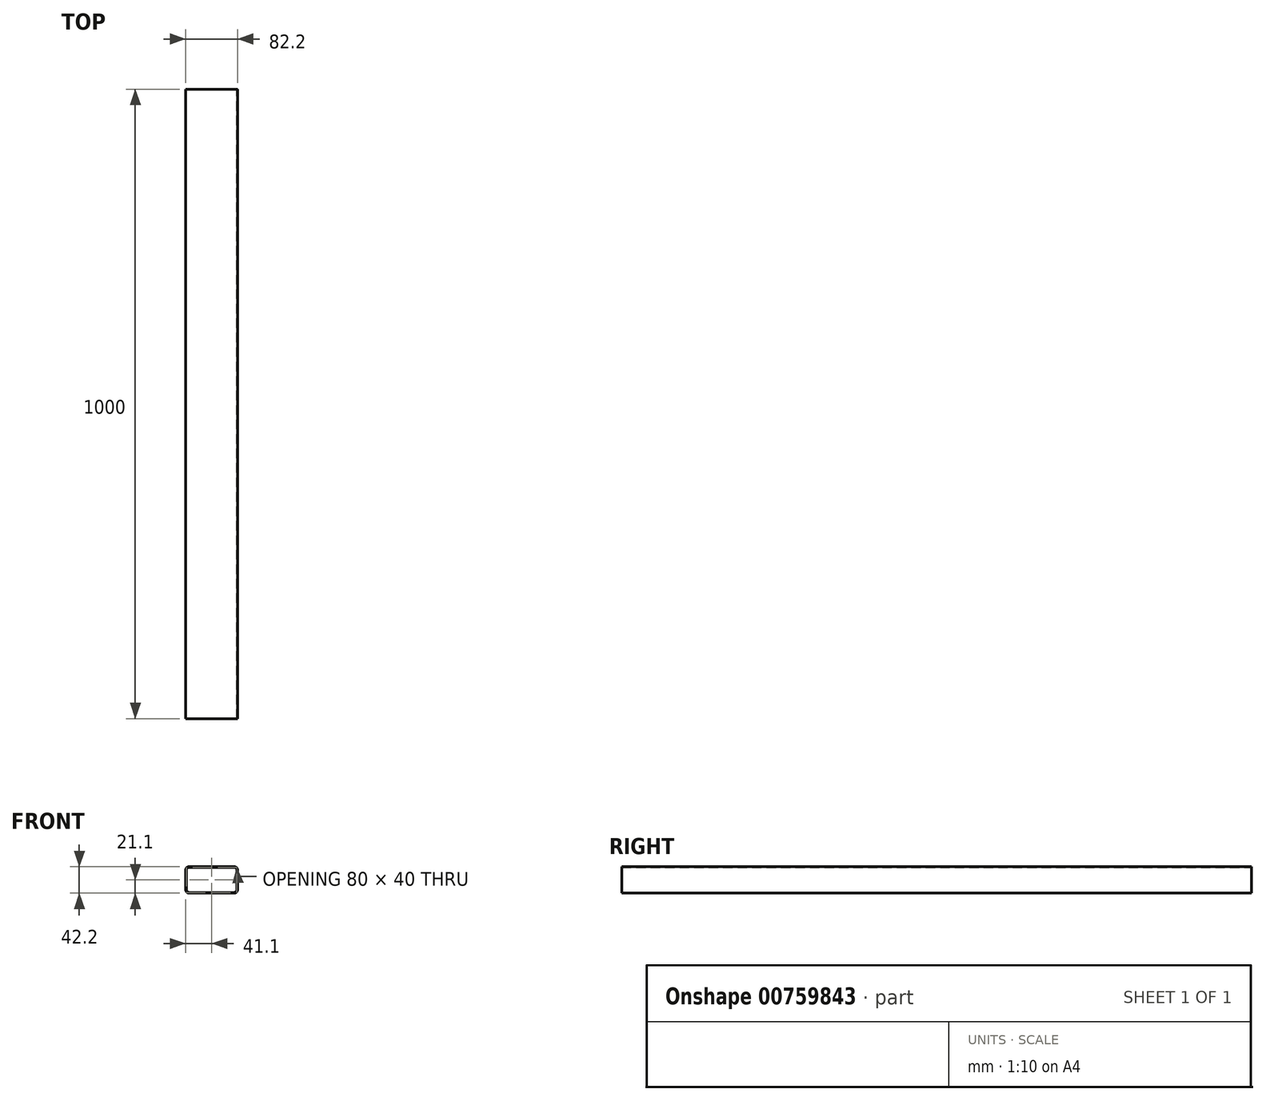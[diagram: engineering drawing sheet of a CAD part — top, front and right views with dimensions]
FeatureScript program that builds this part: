
annotation { "Feature Type Name" : "Feature", "Feature Type Description" : "" }
export const myFeature = defineFeature(function(context is Context, id is Id, definition is map)
    precondition{}
    {
        {
            var Q0;
            Q0=qCreatedBy(makeId("Front.planeOp"),FACE);
            var sketch = newSketch(context, id + "F0", { "sketchPlane" : qUnion([Q0])});
            skLineSegment(sketch, "E0.bottom", {"start": v(-35, 20) * mm, "end": v(35, 20) * mm});
            skLineSegment(sketch, "E0.top", {"start": v(-35, -20) * mm, "end": v(35, -20) * mm});
            skLineSegment(sketch, "E0.left", {"start": v(-40, 15) * mm, "end": v(-40, -15) * mm});
            skLineSegment(sketch, "E0.right", {"start": v(40, 15) * mm, "end": v(40, -15) * mm});
            skPoint(sketch, "E1.visualSharp", {"position": v(-40, 20) * mm});
            skArc(sketch, "E1.filletArc", {"start": v(-35, 20) * mm, "mid": v(-38.54, 18.54) * mm, "end": v(-40, 15) * mm});
            skPoint(sketch, "E2.visualSharp", {"position": v(40, 20) * mm});
            skArc(sketch, "E2.filletArc", {"start": v(40, 15) * mm, "mid": v(38.54, 18.54) * mm, "end": v(35, 20) * mm});
            skPoint(sketch, "E3.visualSharp", {"position": v(40, -20) * mm});
            skArc(sketch, "E3.filletArc", {"start": v(35, -20) * mm, "mid": v(38.54, -18.54) * mm, "end": v(40, -15) * mm});
            skPoint(sketch, "E4.visualSharp", {"position": v(-40, -20) * mm});
            skArc(sketch, "E4.filletArc", {"start": v(-40, -15) * mm, "mid": v(-38.54, -18.54) * mm, "end": v(-35, -20) * mm});
            skLineSegment(sketch, "E5.0", {"start": v(41.1, 16.1) * mm, "end": v(41.1, -16.1) * mm});
            skLineSegment(sketch, "E5.1", {"start": v(-36.1, 21.1) * mm, "end": v(36.1, 21.1) * mm});
            skLineSegment(sketch, "E5.2", {"start": v(-41.1, 16.1) * mm, "end": v(-41.1, -16.1) * mm});
            skLineSegment(sketch, "E5.3", {"start": v(-36.1, -21.1) * mm, "end": v(36.1, -21.1) * mm});
            skPoint(sketch, "E6.visualSharp", {"position": v(-41.1, 21.1) * mm});
            skArc(sketch, "E6.filletArc", {"start": v(-36.1, 21.1) * mm, "mid": v(-39.64, 19.64) * mm, "end": v(-41.1, 16.1) * mm});
            skPoint(sketch, "E7.visualSharp", {"position": v(41.1, 21.1) * mm});
            skArc(sketch, "E7.filletArc", {"start": v(41.1, 16.1) * mm, "mid": v(39.64, 19.64) * mm, "end": v(36.1, 21.1) * mm});
            skPoint(sketch, "E8.visualSharp", {"position": v(41.1, -21.1) * mm});
            skArc(sketch, "E8.filletArc", {"start": v(36.1, -21.1) * mm, "mid": v(39.64, -19.64) * mm, "end": v(41.1, -16.1) * mm});
            skPoint(sketch, "E9.visualSharp", {"position": v(-41.1, -21.1) * mm});
            skArc(sketch, "E9.filletArc", {"start": v(-41.1, -16.1) * mm, "mid": v(-39.64, -19.64) * mm, "end": v(-36.1, -21.1) * mm});
            skSolve(sketch);
        }
        {
            var Q0;
            Q0=makeQuery(id+"F0.imprint","IMPRINT",FACE,{"disambiguationData":[TD([[makeQuery(id+"F0.imprint","IMPRINT",EDGE,{"derivedFrom":sQuery(id+"F0.wireOp",EDGE,"E0.bottom")}),1.0]])]});
            extrude(context, id + "F1", {"entities" : qUnion([Q0]), "depth" : 1000 * mm, "offsetDistance" : 25 * mm});
        }
        {
            var Q0;
            Q0=qCreatedBy(makeId("Front.planeOp"),FACE);
            var sketch = newSketch(context, id + "F2", { "sketchPlane" : qUnion([Q0])});
            skPoint(sketch, "E10", {"position": v(0, 0) * mm});
            skSolve(sketch);
        }
        {
            var Q0;
            Q0=makeQuery(id+"F1.opExtrude","CAP_FACE",FACE,{"disambiguationData":[OSD([sQuery(id+"F0.wireOp",EDGE,"E0.bottom"),sQuery(id+"F0.wireOp",EDGE,"E0.top"),sQuery(id+"F0.wireOp",EDGE,"E0.left"),sQuery(id+"F0.wireOp",EDGE,"E0.right"),sQuery(id+"F0.wireOp",EDGE,"E1.filletArc"),sQuery(id+"F0.wireOp",EDGE,"E2.filletArc"),sQuery(id+"F0.wireOp",EDGE,"E3.filletArc"),sQuery(id+"F0.wireOp",EDGE,"E4.filletArc"),sQuery(id+"F0.wireOp",EDGE,"E5.0"),sQuery(id+"F0.wireOp",EDGE,"E5.1"),sQuery(id+"F0.wireOp",EDGE,"E5.2"),sQuery(id+"F0.wireOp",EDGE,"E5.3"),sQuery(id+"F0.wireOp",EDGE,"E6.filletArc"),sQuery(id+"F0.wireOp",EDGE,"E7.filletArc"),sQuery(id+"F0.wireOp",EDGE,"E8.filletArc"),sQuery(id+"F0.wireOp",EDGE,"E9.filletArc")])],"isStart":false});
            var sketch = newSketch(context, id + "F3", { "sketchPlane" : qUnion([Q0])});
            skPoint(sketch, "E11", {"position": v(0, 0) * mm});
            skSolve(sketch);
        }
    });
